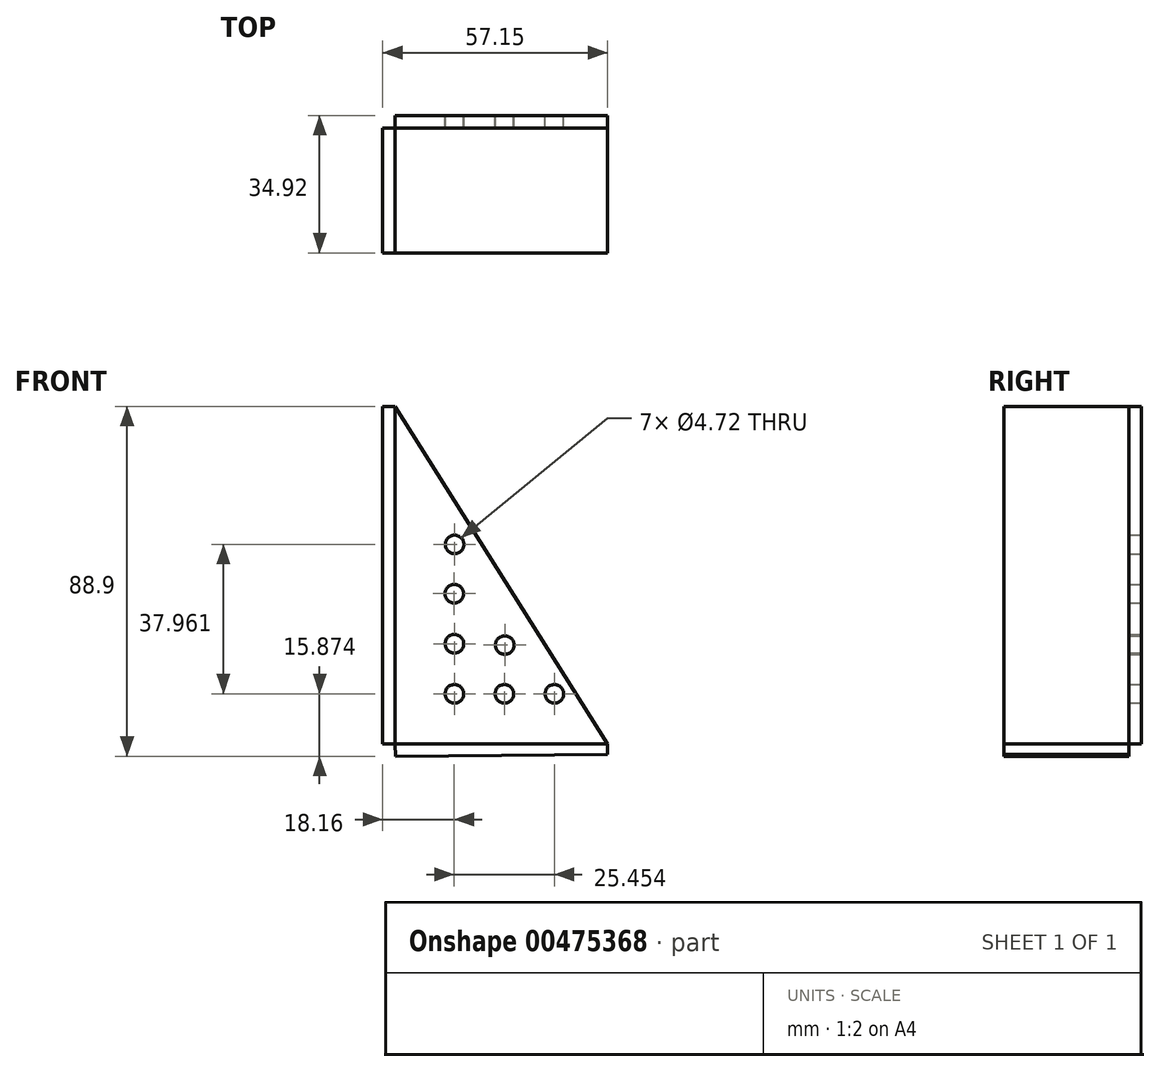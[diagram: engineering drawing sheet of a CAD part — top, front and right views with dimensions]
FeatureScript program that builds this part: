
annotation { "Feature Type Name" : "Feature", "Feature Type Description" : "" }
export const myFeature = defineFeature(function(context is Context, id is Id, definition is map)
    precondition{}
    {
        {
            var Q0;
            Q0=qCreatedBy(makeId("Front.planeOp"),FACE);
            var sketch = newSketch(context, id + "F0", { "sketchPlane" : qUnion([Q0])});
            skLineSegment(sketch, "E0", {"start": v(-17.77, 32.03) * mm, "end": v(-17.77, -53.7) * mm});
            skLineSegment(sketch, "E1", {"start": v(-17.77, -53.7) * mm, "end": v(36.2, -53.7) * mm});
            skLineSegment(sketch, "E2", {"start": v(-17.77, 32.03) * mm, "end": v(36.2, -53.7) * mm});
            skCircle(sketch, "E3", {"center": v(22.67, -41) * mm, "radius": 2.36 * mm});
            skCircle(sketch, "E4", {"center": v(9.97, -41) * mm, "radius": 2.36 * mm});
            skCircle(sketch, "E5", {"center": v(-2.73, -41) * mm, "radius": 2.36 * mm});
            skCircle(sketch, "E6", {"center": v(-2.73, -28.29) * mm, "radius": 2.36 * mm});
            skCircle(sketch, "E7", {"center": v(10.06, -28.6) * mm, "radius": 2.36 * mm});
            skCircle(sketch, "E8", {"center": v(-2.78, -15.55) * mm, "radius": 2.36 * mm});
            skCircle(sketch, "E9", {"center": v(-2.67, -3.04) * mm, "radius": 2.36 * mm});
            skSolve(sketch);
        }
        {
            var Q0;
            Q0 = qSketchRegion(id + "F0", true);
            extrude(context, id + "F1", {"entities" : qUnion([Q0]), "depth" : 3.17 * mm});
        }
        {
            var Q0;
            Q0=makeQuery(id+"F1.opExtrude","CAP_FACE",FACE,{"disambiguationData":[OSD([sQuery(id+"F0.wireOp",EDGE,"E0"),sQuery(id+"F0.wireOp",EDGE,"E1"),sQuery(id+"F0.wireOp",EDGE,"E2"),sQuery(id+"F0.wireOp",EDGE,"E3"),sQuery(id+"F0.wireOp",EDGE,"E4"),sQuery(id+"F0.wireOp",EDGE,"E5"),sQuery(id+"F0.wireOp",EDGE,"E6"),sQuery(id+"F0.wireOp",EDGE,"E7"),sQuery(id+"F0.wireOp",EDGE,"E8"),sQuery(id+"F0.wireOp",EDGE,"E9")])],"isStart":false});
            var sketch = newSketch(context, id + "F2", { "sketchPlane" : qUnion([Q0])});
            skLineSegment(sketch, "E10", {"start": v(-17.77, 32.03) * mm, "end": v(-20.94, 32.03) * mm});
            skLineSegment(sketch, "E11", {"start": v(-20.94, 32.03) * mm, "end": v(-20.94, -53.72) * mm});
            skLineSegment(sketch, "E12", {"start": v(-20.94, -53.72) * mm, "end": v(-17.77, -53.7) * mm});
            skLineSegment(sketch, "E13", {"start": v(-17.77, -53.7) * mm, "end": v(-17.77, 32.03) * mm});
            skLineSegment(sketch, "E14", {"start": v(-17.77, -53.7) * mm, "end": v(-17.74, -56.87) * mm});
            skLineSegment(sketch, "E15", {"start": v(-17.74, -56.87) * mm, "end": v(36.2, -56.44) * mm});
            skLineSegment(sketch, "E16", {"start": v(36.2, -56.44) * mm, "end": v(36.2, -53.7) * mm});
            skLineSegment(sketch, "E17", {"start": v(36.2, -53.7) * mm, "end": v(-17.77, -53.7) * mm});
            skSolve(sketch);
        }
        {
            var Q0;
            Q0=makeQuery(id+"F2.imprint","IMPRINT",FACE,{"disambiguationData":[TD([[makeQuery(id+"F2.imprint","IMPRINT",EDGE,{"derivedFrom":sQuery(id+"F2.wireOp",EDGE,"E14")}),1.0]])]});
            var Q1;
            Q1=makeQuery(id+"F2.imprint","IMPRINT",FACE,{"disambiguationData":[TD([[makeQuery(id+"F2.imprint","IMPRINT",EDGE,{"derivedFrom":sQuery(id+"F2.wireOp",EDGE,"E10")}),1.0]])]});
            extrude(context, id + "F3", {"entities" : qUnion([Q0, Q1]), "depth" : 31.75 * mm});
        }
    });
